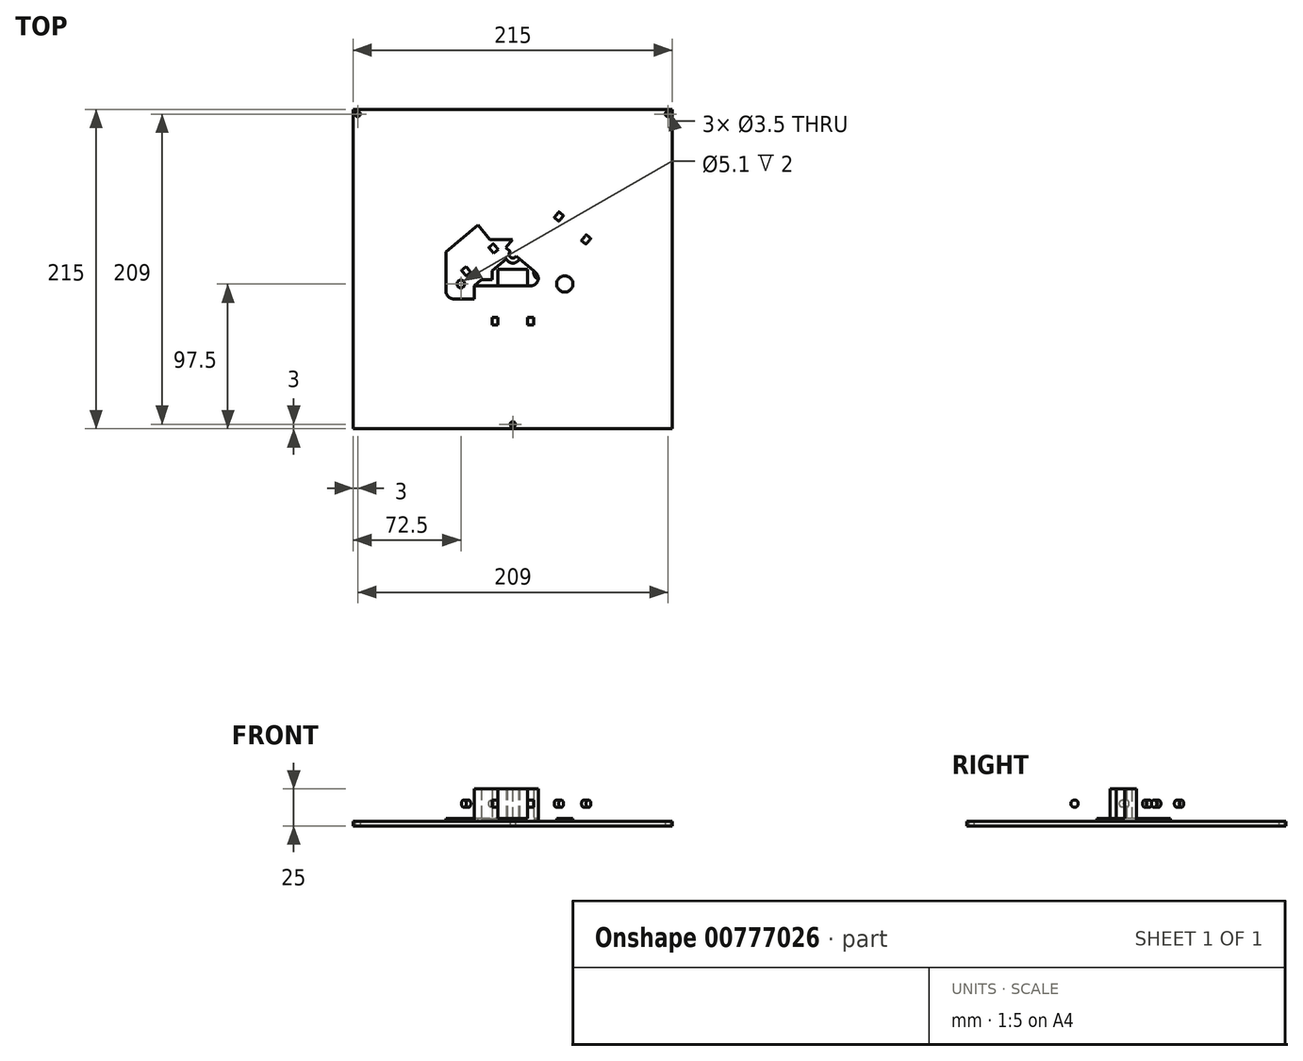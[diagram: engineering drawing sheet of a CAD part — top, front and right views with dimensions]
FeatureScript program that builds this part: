
annotation { "Feature Type Name" : "Feature", "Feature Type Description" : "" }
export const myFeature = defineFeature(function(context is Context, id is Id, definition is map)
    precondition{}
    {
        {
            var Q0;
            Q0=qCreatedBy(makeId("Top.planeOp"),FACE);
            var sketch = newSketch(context, id + "F0", { "sketchPlane" : qUnion([Q0])});
            skLineSegment(sketch, "E0.bottom", {"start": v(-107.5, 107.5) * mm, "end": v(107.5, 107.5) * mm});
            skLineSegment(sketch, "E0.top", {"start": v(-107.5, -107.5) * mm, "end": v(107.5, -107.5) * mm});
            skLineSegment(sketch, "E0.left", {"start": v(-107.5, 107.5) * mm, "end": v(-107.5, -107.5) * mm});
            skLineSegment(sketch, "E0.right", {"start": v(107.5, 107.5) * mm, "end": v(107.5, -107.5) * mm});
            skCircle(sketch, "E1", {"center": v(-104.5, 104.5) * mm, "radius": 1.75 * mm});
            skCircle(sketch, "E2", {"center": v(0, -104.5) * mm, "radius": 1.75 * mm});
            skCircle(sketch, "E3.MirrorC", {"center": v(104.5, 104.5) * mm, "radius": 1.75 * mm});
            skSolve(sketch);
        }
        {
            var Q0;
            Q0=makeQuery(id+"F0.imprint","IMPRINT",FACE,{"disambiguationData":[TD([[makeQuery(id+"F0.imprint","IMPRINT",EDGE,{"derivedFrom":sQuery(id+"F0.wireOp",EDGE,"E0.bottom")}),-1.0]])]});
            extrude(context, id + "F1", {"entities" : qUnion([Q0]), "depth" : 3 * mm, "offsetDistance" : 25 * mm});
        }
        {
            var Q0;
            Q0=qCreatedBy(makeId("Top.planeOp"),FACE);
            var sketch = newSketch(context, id + "F2", { "sketchPlane" : qUnion([Q0])});
            skLineSegment(sketch, "E4.bottom", {"start": v(-45, 20) * mm, "end": v(45, 20) * mm});
            skLineSegment(sketch, "E4.top", {"start": v(-45, -20) * mm, "end": v(45, -20) * mm});
            skLineSegment(sketch, "E4.left", {"start": v(-45, 20) * mm, "end": v(-45, -20) * mm});
            skLineSegment(sketch, "E4.right", {"start": v(45, 20) * mm, "end": v(45, -20) * mm});
            skCircle(sketch, "E5.0", {"center": v(-104.5, 104.5) * mm, "radius": 1.75 * mm});
            skCircle(sketch, "E6.0", {"center": v(104.5, 104.5) * mm, "radius": 1.75 * mm});
            skCircle(sketch, "E7.0", {"center": v(0, -104.5) * mm, "radius": 1.75 * mm});
            skLineSegment(sketch, "E8", {"start": v(0, 0) * mm, "end": v(0, -104.5) * mm, "construction": true});
            skLineSegment(sketch, "E9", {"start": v(-45, 10) * mm, "end": v(45, 10) * mm, "construction": true});
            skCircle(sketch, "E10", {"center": v(-35, -10) * mm, "radius": 2.55 * mm});
            skCircle(sketch, "E11", {"center": v(0, 10) * mm, "radius": 2.55 * mm});
            skLineSegment(sketch, "E12", {"start": v(-17, 0) * mm, "end": v(17, 0) * mm, "construction": true});
            skLineSegment(sketch, "E13", {"start": v(-104.5, 104.5) * mm, "end": v(-17, 0) * mm, "construction": true});
            skLineSegment(sketch, "E14", {"start": v(17, 0) * mm, "end": v(104.5, 104.5) * mm, "construction": true});
            skCircle(sketch, "E15.MirrorC", {"center": v(35, -10) * mm, "radius": 2.55 * mm});
            skLineSegment(sketch, "E16.bottom", {"start": v(-10, 0) * mm, "end": v(10, 0) * mm});
            skLineSegment(sketch, "E16.top", {"start": v(-10, -40) * mm, "end": v(10, -40) * mm});
            skLineSegment(sketch, "E16.left", {"start": v(-10, 0) * mm, "end": v(-10, -40) * mm});
            skLineSegment(sketch, "E16.right", {"start": v(10, 0) * mm, "end": v(10, -40) * mm});
            skLineSegment(sketch, "E17.bottom", {"start": v(-14, 0) * mm, "end": v(14, 0) * mm});
            skLineSegment(sketch, "E17.top", {"start": v(-14, -40) * mm, "end": v(14, -40) * mm});
            skLineSegment(sketch, "E17.left", {"start": v(-14, 0) * mm, "end": v(-14, -40) * mm});
            skLineSegment(sketch, "E17.right", {"start": v(14, 0) * mm, "end": v(14, -40) * mm});
            skLineSegment(sketch, "E18", {"start": v(35.74, 37.96) * mm, "end": v(10.07, 7.3) * mm});
            skLineSegment(sketch, "E19", {"start": v(51.08, 25.12) * mm, "end": v(25.4, -5.55) * mm});
            skLineSegment(sketch, "E20", {"start": v(32.68, 40.53) * mm, "end": v(2.09, 4) * mm});
            skLineSegment(sketch, "E21", {"start": v(32.68, 40.53) * mm, "end": v(54.15, 22.56) * mm});
            skLineSegment(sketch, "E22", {"start": v(54.15, 22.56) * mm, "end": v(28.47, -8.11) * mm});
            skCircle(sketch, "E23", {"center": v(0, 10) * mm, "radius": 5.5 * mm});
            skCircle(sketch, "E24", {"center": v(-35, -10) * mm, "radius": 5.5 * mm});
            skCircle(sketch, "E25.MirrorC", {"center": v(35, -10) * mm, "radius": 5.5 * mm});
            skLineSegment(sketch, "E26.top", {"start": v(-14, 4) * mm, "end": v(14, 4) * mm});
            skLineSegment(sketch, "E26.left", {"start": v(-14, 0) * mm, "end": v(-14, 4) * mm});
            skLineSegment(sketch, "E26.right", {"start": v(14, 0) * mm, "end": v(14, 4) * mm});
            skLineSegment(sketch, "E27", {"start": v(25.4, -5.55) * mm, "end": v(10.07, 7.3) * mm});
            skLineSegment(sketch, "E28", {"start": v(28.47, -8.11) * mm, "end": v(25.9, -11.18) * mm});
            skLineSegment(sketch, "E29", {"start": v(25.9, -11.18) * mm, "end": v(14, -1.22) * mm});
            skPoint(sketch, "E29.endSnap0", {"position": v(14, 2) * mm});
            skLineSegment(sketch, "E30", {"start": v(25.9, -11.18) * mm, "end": v(14, -11.18) * mm});
            skLineSegment(sketch, "E31", {"start": v(21.12, -7.18) * mm, "end": v(14, -7.18) * mm});
            skLineSegment(sketch, "E32.MirrorCS", {"start": v(-32.68, 40.53) * mm, "end": v(-2.09, 4) * mm});
            skLineSegment(sketch, "E33.MirrorCS", {"start": v(-35.74, 37.96) * mm, "end": v(-10.07, 7.3) * mm});
            skLineSegment(sketch, "E34.MirrorCS", {"start": v(-32.68, 40.53) * mm, "end": v(-54.15, 22.56) * mm});
            skLineSegment(sketch, "E35.MirrorCS", {"start": v(-51.08, 25.12) * mm, "end": v(-25.4, -5.55) * mm});
            skLineSegment(sketch, "E36.MirrorCS", {"start": v(-54.15, 22.56) * mm, "end": v(-28.47, -8.11) * mm});
            skLineSegment(sketch, "E37.MirrorCS", {"start": v(-25.4, -5.55) * mm, "end": v(-10.07, 7.3) * mm});
            skLineSegment(sketch, "E38.MirrorCS", {"start": v(-25.9, -11.18) * mm, "end": v(-14, -1.22) * mm});
            skLineSegment(sketch, "E39.MirrorCS", {"start": v(-21.12, -7.18) * mm, "end": v(-14, -7.18) * mm});
            skLineSegment(sketch, "E40.MirrorCS", {"start": v(-25.9, -11.18) * mm, "end": v(-14, -11.18) * mm});
            skLineSegment(sketch, "E41.MirrorCS", {"start": v(45, -10) * mm, "end": v(-45, -10) * mm, "construction": true});
            skLineSegment(sketch, "E42.MirrorCS", {"start": v(-28.47, -8.11) * mm, "end": v(-25.9, -11.18) * mm});
            skPoint(sketch, "E43.orphan", {"position": v(-28.47, -8.11) * mm});
            skSolve(sketch);
        }
        {
            var Q0;
            {var subQ0=sQuery(id+"F2.wireOp",EDGE,"E32.MirrorCS");var subQ1=sQuery(id+"F2.wireOp",EDGE,"E4.bottom");var subQ2=makeQuery(id+"F2.imprint","INTERSECT",VERTEX,{"derivedFrom":[subQ1,subQ0]});Q0=makeQuery(id+"F2.imprint","IMPRINT",FACE,{"disambiguationData":[TD([[makeQuery(id+"F2.imprint","IMPRINT",EDGE,{"disambiguationData":[TD([[subQ2,1.0]])],"derivedFrom":subQ1}),1.0]])]});}
            var Q1;
            {var subQ0=sQuery(id+"F2.wireOp",EDGE,"E32.MirrorCS");var subQ1=sQuery(id+"F2.wireOp",EDGE,"E4.bottom");var subQ2=makeQuery(id+"F2.imprint","INTERSECT",VERTEX,{"derivedFrom":[subQ1,subQ0]});Q1=makeQuery(id+"F2.imprint","IMPRINT",FACE,{"disambiguationData":[TD([[makeQuery(id+"F2.imprint","IMPRINT",EDGE,{"disambiguationData":[TD([[subQ2,1.0]])],"derivedFrom":subQ1}),-1.0]])]});}
            var Q2;
            {var subQ0=sQuery(id+"F2.wireOp",EDGE,"E26.left");Q2=makeQuery(id+"F2.imprint","IMPRINT",FACE,{"disambiguationData":[TD([[makeQuery(id+"F2.imprint","IMPRINT",EDGE,{"derivedFrom":subQ0}),1.0]])]});}
            var Q3;
            {var subQ0=sQuery(id+"F2.wireOp",EDGE,"E36.MirrorCS");var subQ1=sQuery(id+"F2.wireOp",EDGE,"E4.left");var subQ2=makeQuery(id+"F2.imprint","INTERSECT",VERTEX,{"derivedFrom":[subQ1,subQ0]});Q3=makeQuery(id+"F2.imprint","IMPRINT",FACE,{"disambiguationData":[TD([[makeQuery(id+"F2.imprint","IMPRINT",EDGE,{"disambiguationData":[TD([[subQ2,1.0]])],"derivedFrom":subQ1}),-1.0]])]});}
            var Q4;
            {var subQ0=sQuery(id+"F2.wireOp",EDGE,"E26.left");Q4=makeQuery(id+"F2.imprint","IMPRINT",FACE,{"disambiguationData":[TD([[makeQuery(id+"F2.imprint","IMPRINT",EDGE,{"derivedFrom":subQ0}),-1.0]])]});}
            var Q5;
            {var subQ0=sQuery(id+"F2.wireOp",EDGE,"E39.MirrorCS");Q5=makeQuery(id+"F2.imprint","IMPRINT",FACE,{"disambiguationData":[TD([[makeQuery(id+"F2.imprint","IMPRINT",EDGE,{"derivedFrom":subQ0}),-1.0]])]});}
            var Q6;
            {var subQ3=sQuery(id+"F2.wireOp",EDGE,"E17.bottom");var subQ5=sQuery(id+"F2.wireOp",EDGE,"E16.left");var subQ6=makeQuery(id+"F2.imprint","INTERSECT",VERTEX,{"derivedFrom":[subQ5,subQ3]});Q6=makeQuery(id+"F2.imprint","IMPRINT",FACE,{"disambiguationData":[TD([[makeQuery(id+"F2.imprint","IMPRINT",EDGE,{"disambiguationData":[TD([[subQ6,-1.0]])],"derivedFrom":subQ5}),-1.0]])]});}
            var Q7;
            {var subQ3=sQuery(id+"F2.wireOp",EDGE,"E17.bottom");var subQ4=sQuery(id+"F2.wireOp",EDGE,"E16.right");var subQ5=makeQuery(id+"F2.imprint","INTERSECT",VERTEX,{"derivedFrom":[subQ4,subQ3]});Q7=makeQuery(id+"F2.imprint","IMPRINT",FACE,{"disambiguationData":[TD([[makeQuery(id+"F2.imprint","IMPRINT",EDGE,{"disambiguationData":[TD([[subQ5,-1.0]])],"derivedFrom":subQ4}),1.0]])]});}
            var Q8;
            {var subQ3=sQuery(id+"F2.wireOp",EDGE,"E16.right");var subQ5=sQuery(id+"F2.wireOp",EDGE,"E17.top");var subQ6=makeQuery(id+"F2.imprint","INTERSECT",VERTEX,{"derivedFrom":[subQ3,subQ5]});Q8=makeQuery(id+"F2.imprint","IMPRINT",FACE,{"disambiguationData":[TD([[makeQuery(id+"F2.imprint","IMPRINT",EDGE,{"disambiguationData":[TD([[subQ6,1.0]])],"derivedFrom":subQ3}),1.0]])]});}
            var Q9;
            {var subQ3=sQuery(id+"F2.wireOp",EDGE,"E16.left");var subQ5=sQuery(id+"F2.wireOp",EDGE,"E17.top");var subQ6=makeQuery(id+"F2.imprint","INTERSECT",VERTEX,{"derivedFrom":[subQ3,subQ5]});Q9=makeQuery(id+"F2.imprint","IMPRINT",FACE,{"disambiguationData":[TD([[makeQuery(id+"F2.imprint","IMPRINT",EDGE,{"disambiguationData":[TD([[subQ6,1.0]])],"derivedFrom":subQ3}),-1.0]])]});}
            var Q10;
            {var subQ0=sQuery(id+"F2.wireOp",EDGE,"E30");Q10=makeQuery(id+"F2.imprint","IMPRINT",FACE,{"disambiguationData":[TD([[makeQuery(id+"F2.imprint","IMPRINT",EDGE,{"derivedFrom":subQ0}),-1.0]])]});}
            var Q11;
            {var subQ5=sQuery(id+"F2.wireOp",EDGE,"E26.right");Q11=makeQuery(id+"F2.imprint","IMPRINT",FACE,{"disambiguationData":[TD([[makeQuery(id+"F2.imprint","IMPRINT",EDGE,{"derivedFrom":subQ5}),-1.0]])]});}
            var Q12;
            {var subQ1=sQuery(id+"F2.wireOp",EDGE,"E20");var subQ5=sQuery(id+"F2.wireOp",EDGE,"E4.bottom");var subQ6=makeQuery(id+"F2.imprint","INTERSECT",VERTEX,{"derivedFrom":[subQ5,subQ1]});Q12=makeQuery(id+"F2.imprint","IMPRINT",FACE,{"disambiguationData":[TD([[makeQuery(id+"F2.imprint","IMPRINT",EDGE,{"disambiguationData":[TD([[subQ6,-1.0]])],"derivedFrom":subQ5}),-1.0]])]});}
            var Q13;
            {var subQ0=sQuery(id+"F2.wireOp",EDGE,"E20");var subQ1=sQuery(id+"F2.wireOp",EDGE,"E4.bottom");var subQ2=makeQuery(id+"F2.imprint","INTERSECT",VERTEX,{"derivedFrom":[subQ1,subQ0]});Q13=makeQuery(id+"F2.imprint","IMPRINT",FACE,{"disambiguationData":[TD([[makeQuery(id+"F2.imprint","IMPRINT",EDGE,{"disambiguationData":[TD([[subQ2,-1.0]])],"derivedFrom":subQ1}),1.0]])]});}
            var Q14;
            {var subQ0=sQuery(id+"F2.wireOp",EDGE,"E22");var subQ1=sQuery(id+"F2.wireOp",EDGE,"E4.right");var subQ2=makeQuery(id+"F2.imprint","INTERSECT",VERTEX,{"derivedFrom":[subQ1,subQ0]});Q14=makeQuery(id+"F2.imprint","IMPRINT",FACE,{"disambiguationData":[TD([[makeQuery(id+"F2.imprint","IMPRINT",EDGE,{"disambiguationData":[TD([[subQ2,1.0]])],"derivedFrom":subQ1}),1.0]])]});}
            extrude(context, id + "F3", {"entities" : qUnion([Q0, Q1, Q2, Q3, Q4, Q5, Q6, Q7, Q8, Q9, Q10, Q11, Q12, Q13, Q14]), "depth" : 20 * mm, "offsetDistance" : 25 * mm});
        }
        {
            var Q0;
            {var subQ5=sQuery(id+"F2.wireOp",EDGE,"E4.bottom");var subQ7=sQuery(id+"F2.wireOp",EDGE,"E4.left");var subQ8=makeQuery(id+"F2.imprint","INTERSECT",VERTEX,{"derivedFrom":[subQ5,subQ7]});Q0=makeQuery(id+"F2.imprint","IMPRINT",FACE,{"disambiguationData":[TD([[makeQuery(id+"F2.imprint","IMPRINT",EDGE,{"disambiguationData":[TD([[subQ8,-1.0]])],"derivedFrom":subQ5}),1.0]])]});}
            var Q1;
            Q1=makeQuery(id+"F3.opExtrude","CAP_FACE",FACE,{"disambiguationData":[OSD([sQuery(id+"F2.wireOp",EDGE,"E16.left"),sQuery(id+"F2.wireOp",EDGE,"E16.right"),sQuery(id+"F2.wireOp",EDGE,"E17.top"),sQuery(id+"F2.wireOp",EDGE,"E17.left"),sQuery(id+"F2.wireOp",EDGE,"E17.right"),sQuery(id+"F2.wireOp",EDGE,"E18"),sQuery(id+"F2.wireOp",EDGE,"E19"),sQuery(id+"F2.wireOp",EDGE,"E20"),sQuery(id+"F2.wireOp",EDGE,"E21"),sQuery(id+"F2.wireOp",EDGE,"E22"),sQuery(id+"F2.wireOp",EDGE,"E23"),sQuery(id+"F2.wireOp",EDGE,"E17.bottom"),sQuery(id+"F2.wireOp",EDGE,"E26.top"),sQuery(id+"F2.wireOp",EDGE,"E27"),sQuery(id+"F2.wireOp",EDGE,"E28"),sQuery(id+"F2.wireOp",EDGE,"E29"),sQuery(id+"F2.wireOp",EDGE,"E30"),sQuery(id+"F2.wireOp",EDGE,"E31"),sQuery(id+"F2.wireOp",EDGE,"E32.MirrorCS"),sQuery(id+"F2.wireOp",EDGE,"E33.MirrorCS"),sQuery(id+"F2.wireOp",EDGE,"E34.MirrorCS"),sQuery(id+"F2.wireOp",EDGE,"E35.MirrorCS"),sQuery(id+"F2.wireOp",EDGE,"E36.MirrorCS"),sQuery(id+"F2.wireOp",EDGE,"E37.MirrorCS"),sQuery(id+"F2.wireOp",EDGE,"E38.MirrorCS"),sQuery(id+"F2.wireOp",EDGE,"E39.MirrorCS"),sQuery(id+"F2.wireOp",EDGE,"E40.MirrorCS"),sQuery(id+"F2.wireOp",EDGE,"E42.MirrorCS")])],"isStart":false});
            var Q2;
            Q2=makeQuery(id+"F2.imprint","IMPRINT",FACE,{"disambiguationData":[TD([[makeQuery(id+"F2.imprint","IMPRINT",EDGE,{"derivedFrom":sQuery(id+"F2.wireOp",EDGE,"E24")}),-1.0]])]});
            var Q3;
            Q3=makeQuery(id+"F2.imprint","IMPRINT",FACE,{"disambiguationData":[TD([[makeQuery(id+"F2.imprint","IMPRINT",EDGE,{"derivedFrom":sQuery(id+"F2.wireOp",EDGE,"E10")}),-1.0]])]});
            var Q4;
            {var subQ3=sQuery(id+"F2.wireOp",EDGE,"E39.MirrorCS");Q4=makeQuery(id+"F2.imprint","IMPRINT",FACE,{"disambiguationData":[TD([[makeQuery(id+"F2.imprint","IMPRINT",EDGE,{"derivedFrom":subQ3}),1.0]])]});}
            var Q5;
            {var subQ3=sQuery(id+"F2.wireOp",EDGE,"E4.left");var subQ7=sQuery(id+"F2.wireOp",EDGE,"E4.bottom");var subQ9=makeQuery(id+"F2.imprint","INTERSECT",VERTEX,{"derivedFrom":[subQ7,subQ3]});Q5=makeQuery(id+"F2.imprint","IMPRINT",FACE,{"disambiguationData":[TD([[makeQuery(id+"F2.imprint","IMPRINT",EDGE,{"disambiguationData":[TD([[subQ9,-1.0]])],"derivedFrom":subQ7}),-1.0]])]});}
            var Q6;
            {var subQ0=sQuery(id+"F2.wireOp",EDGE,"E16.left");var subQ1=sQuery(id+"F2.wireOp",EDGE,"E4.top");var subQ2=makeQuery(id+"F2.imprint","INTERSECT",VERTEX,{"derivedFrom":[subQ1,subQ0]});Q6=makeQuery(id+"F2.imprint","IMPRINT",FACE,{"disambiguationData":[TD([[makeQuery(id+"F2.imprint","IMPRINT",EDGE,{"disambiguationData":[TD([[subQ2,-1.0]])],"derivedFrom":subQ1}),-1.0]])]});}
            var Q7;
            Q7=makeQuery(id+"F2.imprint","IMPRINT",FACE,{"disambiguationData":[TD([[makeQuery(id+"F2.imprint","IMPRINT",EDGE,{"derivedFrom":sQuery(id+"F2.wireOp",EDGE,"E25.MirrorC")}),1.0]])]});
            var Q8;
            {var subQ3=sQuery(id+"F2.wireOp",EDGE,"E31");Q8=makeQuery(id+"F2.imprint","IMPRINT",FACE,{"disambiguationData":[TD([[makeQuery(id+"F2.imprint","IMPRINT",EDGE,{"derivedFrom":subQ3}),-1.0]])]});}
            var Q9;
            Q9=makeQuery(id+"F2.imprint","IMPRINT",FACE,{"disambiguationData":[TD([[makeQuery(id+"F2.imprint","IMPRINT",EDGE,{"derivedFrom":sQuery(id+"F2.wireOp",EDGE,"E15.MirrorC")}),1.0]])]});
            var Q10;
            {var subQ3=sQuery(id+"F2.wireOp",EDGE,"E4.right");var subQ7=sQuery(id+"F2.wireOp",EDGE,"E4.bottom");var subQ9=makeQuery(id+"F2.imprint","INTERSECT",VERTEX,{"derivedFrom":[subQ7,subQ3]});Q10=makeQuery(id+"F2.imprint","IMPRINT",FACE,{"disambiguationData":[TD([[makeQuery(id+"F2.imprint","IMPRINT",EDGE,{"disambiguationData":[TD([[subQ9,1.0]])],"derivedFrom":subQ7}),-1.0]])]});}
            var Q11;
            {var subQ0=sQuery(id+"F2.wireOp",EDGE,"E32.MirrorCS");var subQ1=sQuery(id+"F2.wireOp",EDGE,"E4.bottom");var subQ2=makeQuery(id+"F2.imprint","INTERSECT",VERTEX,{"derivedFrom":[subQ1,subQ0]});Q11=makeQuery(id+"F2.imprint","IMPRINT",FACE,{"disambiguationData":[TD([[makeQuery(id+"F2.imprint","IMPRINT",EDGE,{"disambiguationData":[TD([[subQ2,-1.0]])],"derivedFrom":subQ1}),-1.0]])]});}
            var Q12;
            Q12=makeQuery(id+"F2.imprint","IMPRINT",FACE,{"disambiguationData":[TD([[makeQuery(id+"F2.imprint","IMPRINT",EDGE,{"derivedFrom":sQuery(id+"F2.wireOp",EDGE,"E11")}),-1.0]])]});
            var Q13;
            {var subQ0=sQuery(id+"F2.wireOp",EDGE,"E26.top");var subQ1=sQuery(id+"F2.wireOp",EDGE,"E20");var subQ2=makeQuery(id+"F2.imprint","INTERSECT",VERTEX,{"derivedFrom":[subQ1,subQ0]});Q13=makeQuery(id+"F2.imprint","IMPRINT",FACE,{"disambiguationData":[TD([[makeQuery(id+"F2.imprint","IMPRINT",EDGE,{"disambiguationData":[TD([[subQ2,1.0]])],"derivedFrom":subQ1}),-1.0]])]});}
            var Q14;
            {var subQ3=sQuery(id+"F2.wireOp",EDGE,"E4.bottom");var subQ5=sQuery(id+"F2.wireOp",EDGE,"E4.right");var subQ6=makeQuery(id+"F2.imprint","INTERSECT",VERTEX,{"derivedFrom":[subQ3,subQ5]});Q14=makeQuery(id+"F2.imprint","IMPRINT",FACE,{"disambiguationData":[TD([[makeQuery(id+"F2.imprint","IMPRINT",EDGE,{"disambiguationData":[TD([[subQ6,1.0]])],"derivedFrom":subQ3}),1.0]])]});}
            var Q15;
            {var subQ0=sQuery(id+"F2.wireOp",EDGE,"E16.left");var subQ1=sQuery(id+"F2.wireOp",EDGE,"E4.top");var subQ2=makeQuery(id+"F2.imprint","INTERSECT",VERTEX,{"derivedFrom":[subQ1,subQ0]});Q15=makeQuery(id+"F2.imprint","IMPRINT",FACE,{"disambiguationData":[TD([[makeQuery(id+"F2.imprint","IMPRINT",EDGE,{"disambiguationData":[TD([[subQ2,-1.0]])],"derivedFrom":subQ1}),1.0]])]});}
            extrude(context, id + "F4", {"entities" : qUnion([Q0, Q1, Q2, Q3, Q4, Q5, Q6, Q7, Q8, Q9, Q10, Q11, Q12, Q13, Q14, Q15]), "operationType" : NewBodyOperationType.ADD, "depth" : 5 * mm, "offsetDistance" : 25 * mm});
        }
        {
            var Q0;
            {var subQ0=sQuery(id+"F2.wireOp",EDGE,"E17.right");var subQ2=makeQuery(id+"F2.imprint","IMPRINT",EDGE,{"disambiguationData":[TD([[makeQuery(id+"F2.imprint","INTERSECT",VERTEX,{"derivedFrom":[sQuery(id+"F2.wireOp",EDGE,"E17.top"),subQ0]}),1.0]])],"derivedFrom":subQ0});var subQ3=makeQuery(id+"F2.imprint","IMPRINT",EDGE,{"disambiguationData":[TD([[makeQuery(id+"F2.imprint","INTERSECT",VERTEX,{"derivedFrom":[subQ0,sQuery(id+"F2.wireOp",EDGE,"E30")]}),-1.0]])],"derivedFrom":subQ0});Q0=makeQuery(id+"F4.boolean.opBoolean","MERGE",FACE,{"derivedFrom":[makeQuery(id+"F3.opExtrude","SWEPT_FACE",FACE,{"disambiguationData":[OSD([subQ0]),TDD([subQ3,subQ2])]}),makeQuery(id+"F4.opExtrude","SWEPT_FACE",FACE,{"disambiguationData":[OSD([subQ0]),TDD([makeQuery(id+"F3.opExtrude","CAP_EDGE",EDGE,{"disambiguationData":[OSD([subQ0]),TDD([subQ3,subQ2])],"isStart":false})])]})]});}
            var sketch = newSketch(context, id + "F5", { "sketchPlane" : qUnion([Q0])});
            skLineSegment(sketch, "E44", {"start": v(-11.18, 15) * mm, "end": v(-43.4, 15) * mm, "construction": true});
            skCircle(sketch, "E45", {"center": v(-16.18, 15) * mm, "radius": 2.5 * mm});
            skCircle(sketch, "E46", {"center": v(-16.18, 15) * mm, "radius": 5 * mm, "construction": true});
            skLineSegment(sketch, "E47", {"start": v(-25.58, 22.54) * mm, "end": v(-25.58, 10.53) * mm, "construction": true});
            skCircle(sketch, "E48.MirrorC", {"center": v(-34.98, 15) * mm, "radius": 5 * mm, "construction": true});
            skCircle(sketch, "E49.MirrorC", {"center": v(-34.98, 15) * mm, "radius": 2.5 * mm});
            skSolve(sketch);
        }
        {
            var Q0;
            Q0=makeQuery(id+"F5.imprint","IMPRINT",FACE,{"disambiguationData":[TD([[makeQuery(id+"F5.imprint","IMPRINT",EDGE,{"derivedFrom":sQuery(id+"F5.wireOp",EDGE,"E49.MirrorC")}),-1.0]])]});
            var Q1;
            Q1=makeQuery(id+"F5.imprint","IMPRINT",FACE,{"disambiguationData":[TD([[makeQuery(id+"F5.imprint","IMPRINT",EDGE,{"derivedFrom":sQuery(id+"F5.wireOp",EDGE,"E45")}),1.0]])]});
            extrude(context, id + "F6", {"entities" : qUnion([Q0, Q1]), "operationType" : NewBodyOperationType.REMOVE, "oppositeDirection" : true, "depth" : 40 * mm, "offsetDistance" : 25 * mm});
        }
        {
            var Q0;
            {var subQ0=sQuery(id+"F2.wireOp",EDGE,"E28");var subQ1=sQuery(id+"F2.wireOp",EDGE,"E22");Q0=makeQuery(id+"F4.boolean.opBoolean","MERGE",FACE,{"derivedFrom":[makeQuery(id+"F3.opExtrude","SWEPT_FACE",FACE,{"disambiguationData":[OSD([subQ1,subQ0])]}),makeQuery(id+"F4.opExtrude","SWEPT_FACE",FACE,{"disambiguationData":[OSD([subQ1,subQ0]),TDD([makeQuery(id+"F3.opExtrude","CAP_EDGE",EDGE,{"disambiguationData":[OSD([subQ1,subQ0])],"isStart":false})])]})]});}
            var sketch = newSketch(context, id + "F7", { "sketchPlane" : qUnion([Q0])});
            skLineSegment(sketch, "E50", {"start": v(52.05, 15) * mm, "end": v(8.05, 15) * mm, "construction": true});
            skCircle(sketch, "E51", {"center": v(19.05, 15) * mm, "radius": 2.5 * mm});
            skCircle(sketch, "E52", {"center": v(19.05, 15) * mm, "radius": 5 * mm, "construction": true});
            skLineSegment(sketch, "E53", {"start": v(33.05, 25) * mm, "end": v(33.05, 5) * mm, "construction": true});
            skCircle(sketch, "E54.MirrorC", {"center": v(47.05, 15) * mm, "radius": 5 * mm, "construction": true});
            skCircle(sketch, "E55.MirrorC", {"center": v(47.05, 15) * mm, "radius": 2.5 * mm});
            skSolve(sketch);
        }
        {
            var Q0;
            Q0=makeQuery(id+"F7.imprint","IMPRINT",FACE,{"disambiguationData":[TD([[makeQuery(id+"F7.imprint","IMPRINT",EDGE,{"derivedFrom":sQuery(id+"F7.wireOp",EDGE,"E51")}),1.0]])]});
            var Q1;
            Q1=makeQuery(id+"F7.imprint","IMPRINT",FACE,{"disambiguationData":[TD([[makeQuery(id+"F7.imprint","IMPRINT",EDGE,{"derivedFrom":sQuery(id+"F7.wireOp",EDGE,"E55.MirrorC")}),-1.0]])]});
            extrude(context, id + "F8", {"entities" : qUnion([Q0, Q1]), "operationType" : NewBodyOperationType.REMOVE, "oppositeDirection" : true, "depth" : 40 * mm, "offsetDistance" : 25 * mm});
        }
        {
            var Q0;
            {var subQ0=sQuery(id+"F2.wireOp",EDGE,"E42.MirrorCS");var subQ1=sQuery(id+"F2.wireOp",EDGE,"E36.MirrorCS");Q0=makeQuery(id+"F4.boolean.opBoolean","MERGE",FACE,{"derivedFrom":[makeQuery(id+"F3.opExtrude","SWEPT_FACE",FACE,{"disambiguationData":[OSD([subQ1,subQ0])]}),makeQuery(id+"F4.opExtrude","SWEPT_FACE",FACE,{"disambiguationData":[OSD([subQ1,subQ0]),TDD([makeQuery(id+"F3.opExtrude","CAP_EDGE",EDGE,{"disambiguationData":[OSD([subQ1,subQ0])],"isStart":false})])]})]});}
            var sketch = newSketch(context, id + "F9", { "sketchPlane" : qUnion([Q0])});
            skLineSegment(sketch, "E56", {"start": v(-8.05, 15) * mm, "end": v(-52.05, 15) * mm, "construction": true});
            skCircle(sketch, "E57", {"center": v(-47.05, 15) * mm, "radius": 2.5 * mm});
            skCircle(sketch, "E58", {"center": v(-47.05, 15) * mm, "radius": 5 * mm, "construction": true});
            skLineSegment(sketch, "E59", {"start": v(-33.05, 25) * mm, "end": v(-33.05, 5) * mm, "construction": true});
            skCircle(sketch, "E60.MirrorC", {"center": v(-19.05, 15) * mm, "radius": 5 * mm, "construction": true});
            skCircle(sketch, "E61.MirrorC", {"center": v(-19.05, 15) * mm, "radius": 2.5 * mm});
            skSolve(sketch);
        }
        {
            var Q0;
            Q0=makeQuery(id+"F9.imprint","IMPRINT",FACE,{"disambiguationData":[TD([[makeQuery(id+"F9.imprint","IMPRINT",EDGE,{"derivedFrom":sQuery(id+"F9.wireOp",EDGE,"E57")}),1.0]])]});
            var Q1;
            Q1=makeQuery(id+"F9.imprint","IMPRINT",FACE,{"disambiguationData":[TD([[makeQuery(id+"F9.imprint","IMPRINT",EDGE,{"derivedFrom":sQuery(id+"F9.wireOp",EDGE,"E61.MirrorC")}),-1.0]])]});
            extrude(context, id + "F10", {"entities" : qUnion([Q0, Q1]), "operationType" : NewBodyOperationType.REMOVE, "oppositeDirection" : true, "depth" : 40 * mm, "offsetDistance" : 25 * mm});
        }
        {
            var Q0;
            {var subQ0=sQuery(id+"F2.wireOp",EDGE,"E34.MirrorCS");Q0=makeQuery(id+"F4.opExtrude","CAP_EDGE",EDGE,{"disambiguationData":[OSD([subQ0]),TDD([makeQuery(id+"F3.opExtrude","CAP_EDGE",EDGE,{"disambiguationData":[OSD([subQ0]),TDD([makeQuery(id+"F2.imprint","IMPRINT",EDGE,{"disambiguationData":[TD([[makeQuery(id+"F2.imprint","INTERSECT",VERTEX,{"derivedFrom":[sQuery(id+"F2.wireOp",EDGE,"E32.MirrorCS"),subQ0]}),-1.0]])],"derivedFrom":subQ0})])],"isStart":false})])],"isStart":false});}
            var Q1;
            {var subQ0=sQuery(id+"F2.wireOp",EDGE,"E34.MirrorCS");Q1=makeQuery(id+"F4.opExtrude","CAP_EDGE",EDGE,{"disambiguationData":[OSD([subQ0]),TDD([makeQuery(id+"F3.opExtrude","CAP_EDGE",EDGE,{"disambiguationData":[OSD([subQ0]),TDD([makeQuery(id+"F2.imprint","IMPRINT",EDGE,{"disambiguationData":[TD([[makeQuery(id+"F2.imprint","INTERSECT",VERTEX,{"derivedFrom":[subQ0,sQuery(id+"F2.wireOp",EDGE,"E36.MirrorCS")]}),1.0]])],"derivedFrom":subQ0})])],"isStart":false})])],"isStart":false});}
            var Q2;
            {var subQ0=sQuery(id+"F2.wireOp",EDGE,"E17.top");Q2=makeQuery(id+"F4.opExtrude","CAP_EDGE",EDGE,{"disambiguationData":[OSD([subQ0]),TDD([makeQuery(id+"F3.opExtrude","CAP_EDGE",EDGE,{"disambiguationData":[OSD([subQ0]),TDD([makeQuery(id+"F2.imprint","IMPRINT",EDGE,{"disambiguationData":[TD([[makeQuery(id+"F2.imprint","INTERSECT",VERTEX,{"derivedFrom":[sQuery(id+"F2.wireOp",EDGE,"E16.left"),subQ0]}),1.0]])],"derivedFrom":subQ0})])],"isStart":false})])],"isStart":false});}
            var Q3;
            {var subQ0=sQuery(id+"F2.wireOp",EDGE,"E17.top");Q3=makeQuery(id+"F4.opExtrude","CAP_EDGE",EDGE,{"disambiguationData":[OSD([subQ0]),TDD([makeQuery(id+"F3.opExtrude","CAP_EDGE",EDGE,{"disambiguationData":[OSD([subQ0]),TDD([makeQuery(id+"F2.imprint","IMPRINT",EDGE,{"disambiguationData":[TD([[makeQuery(id+"F2.imprint","INTERSECT",VERTEX,{"derivedFrom":[sQuery(id+"F2.wireOp",EDGE,"E16.right"),subQ0]}),-1.0]])],"derivedFrom":subQ0})])],"isStart":false})])],"isStart":false});}
            var Q4;
            {var subQ0=sQuery(id+"F2.wireOp",EDGE,"E21");Q4=makeQuery(id+"F4.opExtrude","CAP_EDGE",EDGE,{"disambiguationData":[OSD([subQ0]),TDD([makeQuery(id+"F3.opExtrude","CAP_EDGE",EDGE,{"disambiguationData":[OSD([subQ0]),TDD([makeQuery(id+"F2.imprint","IMPRINT",EDGE,{"disambiguationData":[TD([[makeQuery(id+"F2.imprint","INTERSECT",VERTEX,{"derivedFrom":[sQuery(id+"F2.wireOp",EDGE,"E18"),subQ0]}),1.0]])],"derivedFrom":subQ0})])],"isStart":false})])],"isStart":false});}
            var Q5;
            Q5=makeQuery(id+"F4.opExtrude","SWEPT_EDGE",EDGE,{"disambiguationData":[OSD([sQuery(id+"F2.wireOp",EDGE,"E4.top"),sQuery(id+"F2.wireOp",EDGE,"E4.left")])]});
            var Q6;
            {var subQ0=sQuery(id+"F2.wireOp",EDGE,"E21");Q6=makeQuery(id+"F4.opExtrude","CAP_EDGE",EDGE,{"disambiguationData":[OSD([subQ0]),TDD([makeQuery(id+"F3.opExtrude","CAP_EDGE",EDGE,{"disambiguationData":[OSD([subQ0]),TDD([makeQuery(id+"F2.imprint","IMPRINT",EDGE,{"disambiguationData":[TD([[makeQuery(id+"F2.imprint","INTERSECT",VERTEX,{"derivedFrom":[sQuery(id+"F2.wireOp",EDGE,"E19"),subQ0]}),-1.0]])],"derivedFrom":subQ0})])],"isStart":false})])],"isStart":false});}
            var Q7;
            {var subQ0=sQuery(id+"F2.wireOp",EDGE,"E42.MirrorCS");var subQ1=sQuery(id+"F2.wireOp",EDGE,"E40.MirrorCS");var subQ2=sQuery(id+"F2.wireOp",EDGE,"E38.MirrorCS");Q7=makeQuery(id+"F4.boolean.opBoolean","MERGE",EDGE,{"derivedFrom":[makeQuery(id+"F3.opExtrude","SWEPT_EDGE",EDGE,{"disambiguationData":[OSD([subQ2,subQ1,subQ0])]}),makeQuery(id+"F4.opExtrude","SWEPT_EDGE",EDGE,{"disambiguationData":[OSD([subQ2,subQ1,subQ0]),TDD([makeQuery(id+"F3.opExtrude","CAP_VERTEX",VERTEX,{"disambiguationData":[OSD([subQ2,subQ1,subQ0])],"isStart":false})])]})]});}
            var Q8;
            {var subQ0=sQuery(id+"F2.wireOp",EDGE,"E30");var subQ1=sQuery(id+"F2.wireOp",EDGE,"E29");var subQ2=sQuery(id+"F2.wireOp",EDGE,"E28");Q8=makeQuery(id+"F4.boolean.opBoolean","MERGE",EDGE,{"derivedFrom":[makeQuery(id+"F3.opExtrude","SWEPT_EDGE",EDGE,{"disambiguationData":[OSD([subQ2,subQ1,subQ0])]}),makeQuery(id+"F4.opExtrude","SWEPT_EDGE",EDGE,{"disambiguationData":[OSD([subQ2,subQ1,subQ0]),TDD([makeQuery(id+"F3.opExtrude","CAP_VERTEX",VERTEX,{"disambiguationData":[OSD([subQ2,subQ1,subQ0])],"isStart":false})])]})]});}
            var Q9;
            {var subQ0=sQuery(id+"F2.wireOp",EDGE,"E26.top");var subQ1=sQuery(id+"F2.wireOp",EDGE,"E20");Q9=makeQuery(id+"F4.boolean.opBoolean","MERGE",EDGE,{"derivedFrom":[makeQuery(id+"F3.opExtrude","SWEPT_EDGE",EDGE,{"disambiguationData":[OSD([subQ1,subQ0])]}),makeQuery(id+"F4.opExtrude","SWEPT_EDGE",EDGE,{"disambiguationData":[OSD([subQ1,subQ0]),TDD([makeQuery(id+"F3.opExtrude","CAP_VERTEX",VERTEX,{"disambiguationData":[OSD([subQ1,subQ0])],"isStart":false})])]})]});}
            var Q10;
            {var subQ0=sQuery(id+"F2.wireOp",EDGE,"E32.MirrorCS");var subQ1=sQuery(id+"F2.wireOp",EDGE,"E26.top");Q10=makeQuery(id+"F4.boolean.opBoolean","MERGE",EDGE,{"derivedFrom":[makeQuery(id+"F3.opExtrude","SWEPT_EDGE",EDGE,{"disambiguationData":[OSD([subQ1,subQ0])]}),makeQuery(id+"F4.opExtrude","SWEPT_EDGE",EDGE,{"disambiguationData":[OSD([subQ1,subQ0]),TDD([makeQuery(id+"F3.opExtrude","CAP_VERTEX",VERTEX,{"disambiguationData":[OSD([subQ1,subQ0])],"isStart":false})])]})]});}
            var Q11;
            Q11=makeQuery(id+"F4.opExtrude","SWEPT_EDGE",EDGE,{"disambiguationData":[OSD([sQuery(id+"F2.wireOp",EDGE,"E4.bottom"),sQuery(id+"F2.wireOp",EDGE,"E32.MirrorCS")])]});
            var Q12;
            Q12=makeQuery(id+"F4.opExtrude","SWEPT_EDGE",EDGE,{"disambiguationData":[OSD([sQuery(id+"F2.wireOp",EDGE,"E4.bottom"),sQuery(id+"F2.wireOp",EDGE,"E20")])]});
            var Q13;
            Q13=makeQuery(id+"F4.opExtrude","SWEPT_EDGE",EDGE,{"disambiguationData":[OSD([sQuery(id+"F2.wireOp",EDGE,"E4.top"),sQuery(id+"F2.wireOp",EDGE,"E4.right")])]});
            var Q14;
            Q14=makeQuery(id+"F4.opExtrude","SWEPT_EDGE",EDGE,{"disambiguationData":[OSD([sQuery(id+"F2.wireOp",EDGE,"E4.right"),sQuery(id+"F2.wireOp",EDGE,"E22")])]});
            var Q15;
            Q15=makeQuery(id+"F4.opExtrude","SWEPT_EDGE",EDGE,{"disambiguationData":[OSD([sQuery(id+"F2.wireOp",EDGE,"E4.top"),sQuery(id+"F2.wireOp",EDGE,"E17.right")])]});
            var Q16;
            Q16=makeQuery(id+"F4.opExtrude","SWEPT_EDGE",EDGE,{"disambiguationData":[OSD([sQuery(id+"F2.wireOp",EDGE,"E4.top"),sQuery(id+"F2.wireOp",EDGE,"E17.left")])]});
            var Q17;
            Q17=makeQuery(id+"F4.opExtrude","SWEPT_EDGE",EDGE,{"disambiguationData":[OSD([sQuery(id+"F2.wireOp",EDGE,"E4.left"),sQuery(id+"F2.wireOp",EDGE,"E36.MirrorCS")])]});
            fillet(context, id + "F11", {"entities" : qUnion([Q0, Q1, Q2, Q3, Q4, Q5, Q6, Q7, Q8, Q9, Q10, Q11, Q12, Q13, Q14, Q15, Q16, Q17]), "radius" : 5 * mm, "tangentPropagation" : true, "allowEdgeOverflow" : false});
        }
    });
